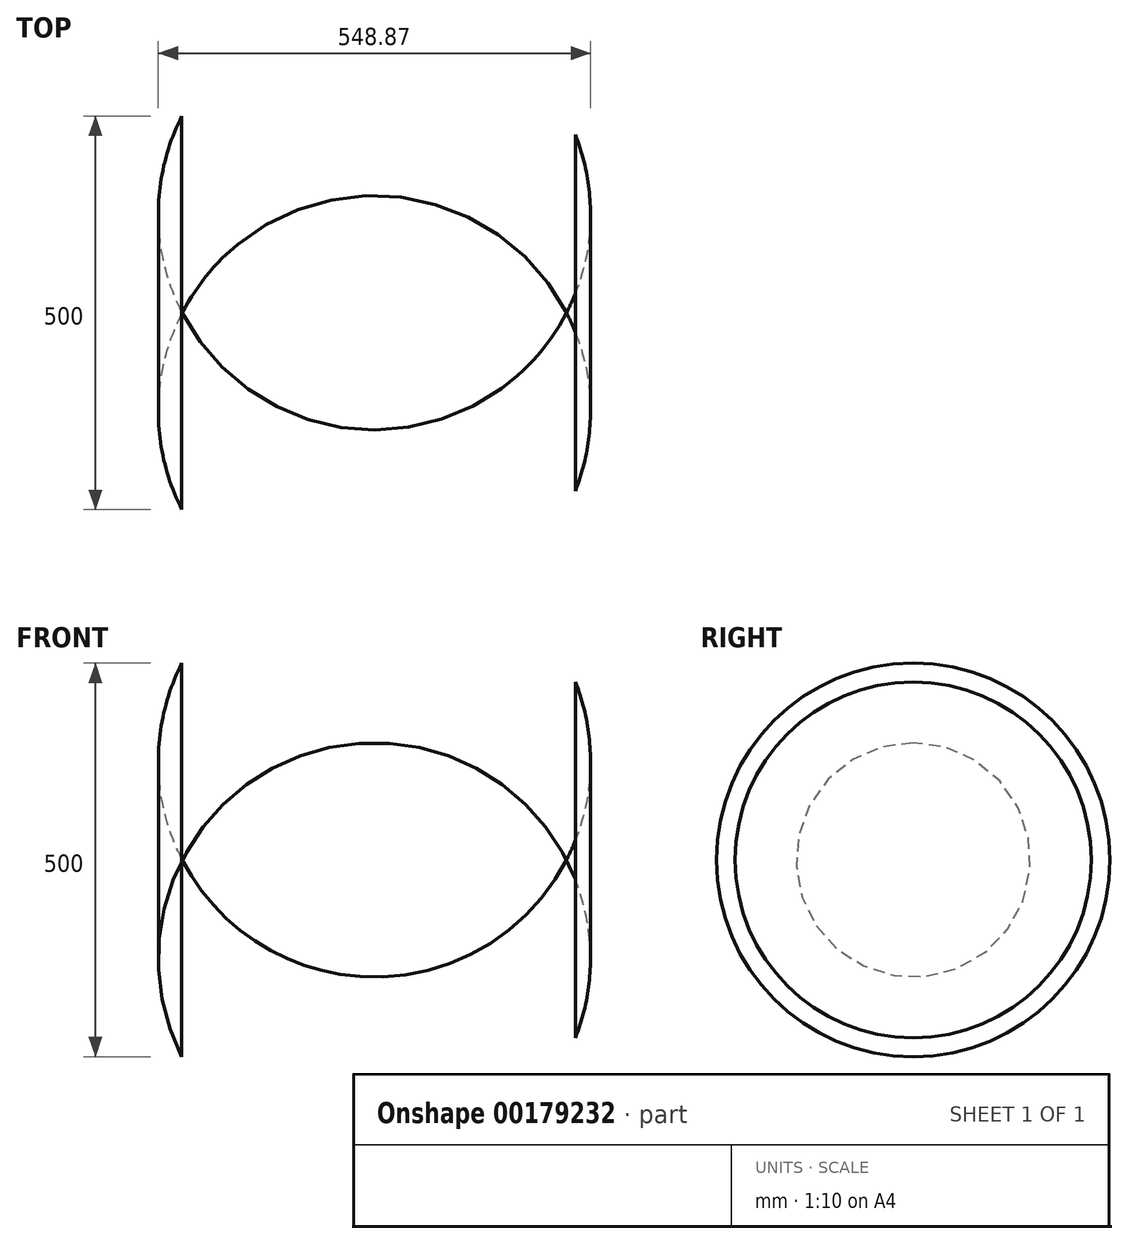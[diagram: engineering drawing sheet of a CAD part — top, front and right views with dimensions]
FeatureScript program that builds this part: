
annotation { "Feature Type Name" : "Feature", "Feature Type Description" : "" }
export const myFeature = defineFeature(function(context is Context, id is Id, definition is map)
    precondition{}
    {
        {
            var Q0;
            Q0=qCreatedBy(makeId("Front.planeOp"),FACE);
            var sketch = newSketch(context, id + "F0", { "sketchPlane" : qUnion([Q0])});
            skLineSegment(sketch, "E0", {"start": v(0, 0) * mm, "end": v(500, 0) * mm, "construction": true});
            skLineSegment(sketch, "E1", {"start": v(0, 0) * mm, "end": v(0, 250) * mm});
            skLineSegment(sketch, "E2", {"start": v(500, 0) * mm, "end": v(500, 226.12) * mm});
            skLineSegment(sketch, "E3", {"start": v(250, 0) * mm, "end": v(250, 400) * mm, "construction": true});
            skArc(sketch, "E4", {"start": v(500, 226.12) * mm, "mid": v(257.72, 399.74) * mm, "end": v(0, 250) * mm});
            skLineSegment(sketch, "E5", {"start": v(500, 0) * mm, "end": v(0, 0) * mm});
            skSolve(sketch);
        }
        {
            var Q0;
            Q0=makeQuery(id+"F0.imprint","IMPRINT",FACE,{"disambiguationData":[TD([[makeQuery(id+"F0.imprint","IMPRINT",EDGE,{"derivedFrom":sQuery(id+"F0.wireOp",EDGE,"E1")}),-1.0]])]});
            var Q1;
            Q1=sQuery(id+"F0.wireOp",EDGE,"E5");
            revolve(context, id + "F1", {"entities" : qUnion([Q0]), "axis" : qUnion([Q1]), "revolveType" : RevolveType.FULL});
        }
    });
